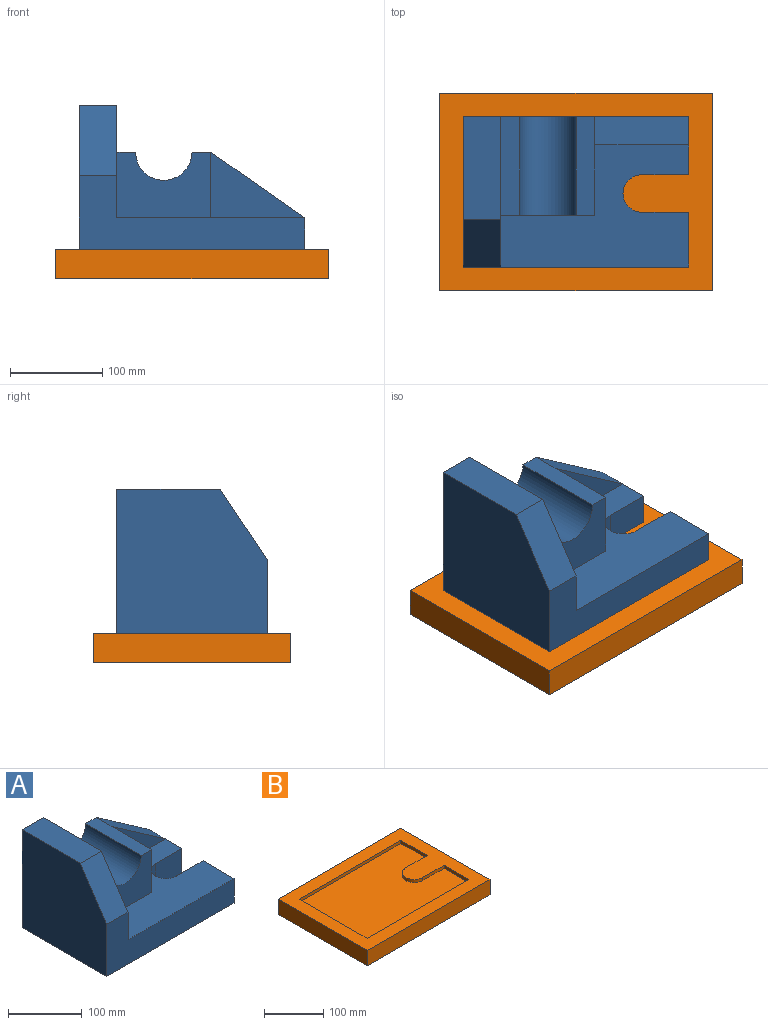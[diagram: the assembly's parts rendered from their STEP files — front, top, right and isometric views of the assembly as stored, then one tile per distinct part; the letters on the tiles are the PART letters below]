
ASSEMBLY  parts=2 mates=1
PART A: 20 faces, bbox 243.8x162.6x162.6 mm
  f0: plane 203.2x132.08mm, normal (0,0,1), area 16383.6mm2, adj f1,f2,f5,f6,f7,f8,f9,f15
  f1: plane 162.56x121.92mm, normal (1,0,0), area 10296.8mm2, adj f0,f3,f5,f11,f12,f14,f17
  f2: plane 62.64x40.64mm, normal (1,0,0), area 2545.7mm2, adj f0,f3,f9,f10,f18
  f3: plane 243.84x162.56mm, normal (0,1,0), area 24243.9mm2, adj f1,f2,f4,f10,f11,f13,f14,f16
  f4: plane 162.56x162.56mm, normal (-1,0,0), area 24490.3mm2, adj f3,f5,f10,f11,f12
  f5: plane 243.84x86.36mm, normal (0,-1,0), area 11767.7mm2, adj f0,f1,f4,f6,f10,f12
  f6: plane 59.28x40.64mm, normal (1,0,0), area 2409.1mm2, adj f0,f5,f7,f10
  f7: plane 50.8x40.64mm, normal (0,1,0), area 2064.5mm2, adj f0,f6,f8,f10
  f8: cylinder r=20.32mm len=40.64mm, axis (0,0,-1), area 2594.3mm2, adj f0,f7,f9,f10
  f9: plane 50.8x40.64mm, normal (0,-1,0), area 2064.5mm2, adj f0,f2,f8,f10
  f10: plane 243.84x162.56mm, normal (0,0,-1), area 36925.5mm2, adj f2,f3,f4,f5,f6,f7,f8,f9
  f11: plane 111.76x40.64mm, normal (0,0,1), area 4541.9mm2, adj f1,f3,f4,f12
  f12: plane 76.2x50.8mm, normal (0,-0.83,0.55), area 3721.9mm2, adj f1,f4,f5,f11
  f13: cylinder r=30.48mm len=106.68mm, axis (0,1,0), area 10215.2mm2, adj f3,f14,f16,f17
  f14: plane 106.68x20.32mm, normal (0,0,1), area 2167.7mm2, adj f1,f3,f13,f17
  f15: plane 76.2x71.12mm, normal (1,0,0), area 5419.3mm2, adj f0,f16,f17,f19
  f16: plane 106.68x20.32mm, normal (0,0,1), area 2167.7mm2, adj f3,f13,f15,f17,f18
  f17: plane 101.6x71.12mm, normal (0,-1,0), area 5766.5mm2, adj f0,f1,f13,f14,f15,f16
  f18: plane 101.6x71.12mm, normal (0.57,0,0.82), area 3780.1mm2, adj f2,f3,f16,f19
  f19: plane 101.6x71.12mm, normal (0,-1,0), area 3612.9mm2, adj f0,f15,f18
PART B: 15 faces, bbox 294.6x213.4x31.8 mm
  f0: plane 294.64x31.75mm, normal (0,1,0), area 9354.8mm2, adj f1,f3,f4,f13
  f1: plane 213.36x31.75mm, normal (-1,0,0), area 6774.2mm2, adj f0,f2,f4,f13
  f2: plane 294.64x31.75mm, normal (0,-1,0), area 9354.8mm2, adj f1,f3,f4,f13
  f3: plane 213.36x31.75mm, normal (1,0,0), area 6774.2mm2, adj f0,f2,f4,f13
  f4: plane 294.64x213.36mm, normal (0,0,-1), area 62864.4mm2, adj f0,f1,f2,f3
  f5: plane 162.56x6.35mm, normal (1,0,0), area 1032.3mm2, adj f6,f12,f13,f14
  f6: plane 243.84x6.35mm, normal (0,-1,0), area 1548.4mm2, adj f5,f7,f13,f14
  f7: plane 62.64x6.35mm, normal (-1,0,0), area 397.8mm2, adj f6,f8,f13,f14
  f8: plane 50.8x6.35mm, normal (0,1,0), area 322.6mm2, adj f7,f9,f13,f14
  f9: cylinder r=20.32mm len=40.64mm, axis (0,0,1), area 405.4mm2, adj f8,f10,f13,f14
  f10: plane 50.8x6.35mm, normal (0,-1,0), area 322.6mm2, adj f9,f11,f13,f14
  f11: plane 59.28x6.35mm, normal (-1,0,0), area 376.4mm2, adj f10,f12,f13,f14
  f12: plane 243.84x6.35mm, normal (0,1,0), area 1548.4mm2, adj f5,f11,f13,f14
  f13: plane 294.64x213.36mm, normal (0,0,1), area 25938.9mm2, adj f0,f1,f2,f3,f5,f6,f7,f8
  f14: plane 243.84x162.56mm, normal (0,0,1), area 36925.5mm2, adj f5,f6,f7,f8,f9,f10,f11,f12
PLACE A t=(-221.25,53.31,-37.21)mm
PLACE B t=(-221.25,53.31,-37.21)mm
MATE parallel B.f14 <-> A.f10  axis (0,0,1) through (-105.82,-27.84,-37.21)mm
